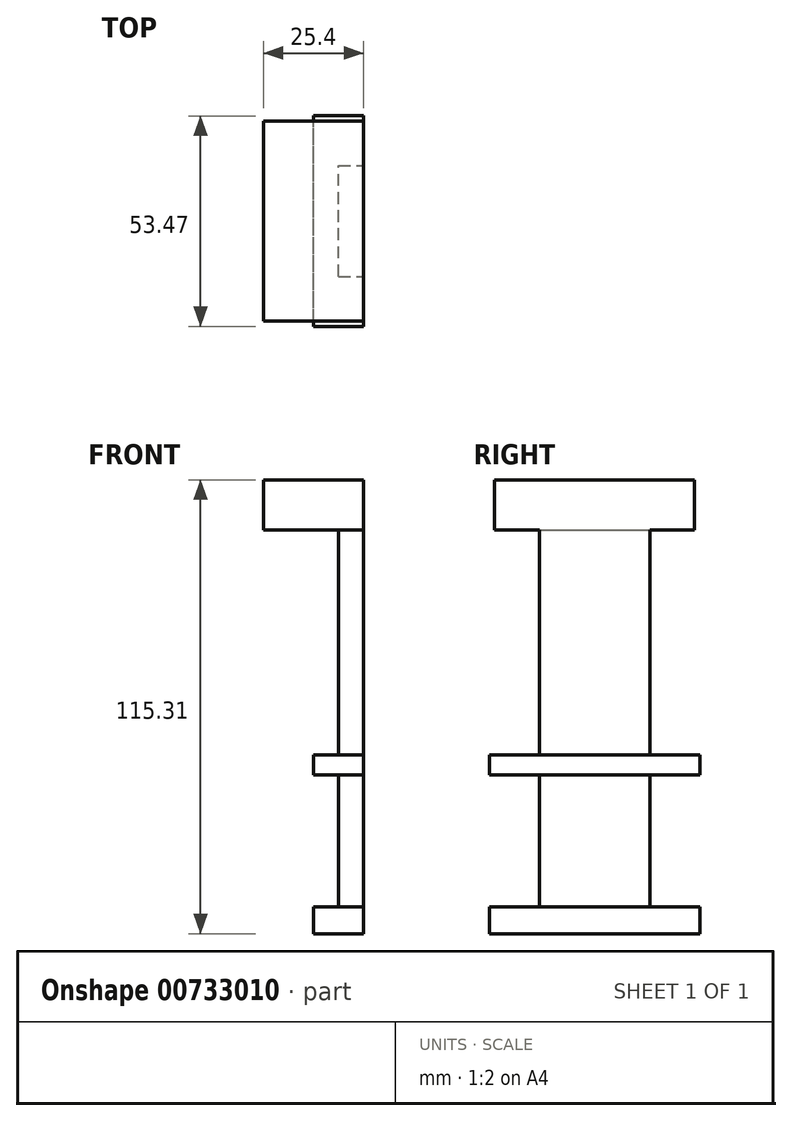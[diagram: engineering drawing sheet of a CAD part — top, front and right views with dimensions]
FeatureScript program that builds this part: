
annotation { "Feature Type Name" : "Feature", "Feature Type Description" : "" }
export const myFeature = defineFeature(function(context is Context, id is Id, definition is map)
    precondition{}
    {
        {
            var Q0;
            Q0=qCreatedBy(makeId("Right.planeOp"),FACE);
            var sketch = newSketch(context, id + "F0", { "sketchPlane" : qUnion([Q0])});
            skLineSegment(sketch, "E0", {"start": v(-21.66, 74) * mm, "end": v(-21.66, 61.3) * mm});
            skLineSegment(sketch, "E1", {"start": v(-21.66, 74) * mm, "end": v(29.14, 74) * mm});
            skLineSegment(sketch, "E2", {"start": v(-21.66, 61.3) * mm, "end": v(29.14, 61.3) * mm});
            skLineSegment(sketch, "E3", {"start": v(29.14, 74) * mm, "end": v(29.14, 61.3) * mm});
            skLineSegment(sketch, "E4", {"start": v(-10.3, 61.3) * mm, "end": v(-10.3, 4.15) * mm});
            skLineSegment(sketch, "E5", {"start": v(17.77, 61.3) * mm, "end": v(17.77, 4.15) * mm});
            skLineSegment(sketch, "E6", {"start": v(-10.3, 4.15) * mm, "end": v(-23, 4.15) * mm});
            skLineSegment(sketch, "E7", {"start": v(-23, 4.15) * mm, "end": v(-23, -0.95) * mm});
            skLineSegment(sketch, "E8", {"start": v(17.77, 4.15) * mm, "end": v(30.47, 4.15) * mm});
            skLineSegment(sketch, "E9", {"start": v(-23, -0.95) * mm, "end": v(30.47, -0.95) * mm});
            skLineSegment(sketch, "E10", {"start": v(30.47, 4.15) * mm, "end": v(30.47, -0.95) * mm});
            skLineSegment(sketch, "E11", {"start": v(-10.3, 4.15) * mm, "end": v(17.77, 4.15) * mm});
            skLineSegment(sketch, "E12", {"start": v(-10.3, -0.95) * mm, "end": v(-10.3, -34.48) * mm});
            skLineSegment(sketch, "E13", {"start": v(17.77, -0.95) * mm, "end": v(17.77, -34.48) * mm});
            skLineSegment(sketch, "E14", {"start": v(-10.3, -34.48) * mm, "end": v(17.77, -34.48) * mm});
            skLineSegment(sketch, "E15", {"start": v(17.77, -34.48) * mm, "end": v(30.47, -34.48) * mm});
            skLineSegment(sketch, "E16", {"start": v(30.47, -34.48) * mm, "end": v(30.47, -41.3) * mm});
            skLineSegment(sketch, "E17", {"start": v(-10.3, -34.48) * mm, "end": v(-23, -34.48) * mm});
            skLineSegment(sketch, "E18", {"start": v(30.47, -41.3) * mm, "end": v(-23, -41.3) * mm});
            skLineSegment(sketch, "E19", {"start": v(-23, -34.48) * mm, "end": v(-23, -41.3) * mm});
            skSolve(sketch);
        }
        {
            var Q0;
            {var subQ3=sQuery(id+"F0.wireOp",EDGE,"E0");Q0=makeQuery(id+"F0.imprint","IMPRINT",FACE,{"disambiguationData":[TD([[makeQuery(id+"F0.imprint","IMPRINT",EDGE,{"derivedFrom":subQ3}),1.0]])]});}
            extrude(context, id + "F1", {"entities" : qUnion([Q0]), "oppositeDirection" : true, "depth" : 25.4 * mm, "offsetDistance" : 25.4 * mm});
        }
        {
            var Q0;
            {var subQ0=sQuery(id+"F0.wireOp",EDGE,"E4");Q0=makeQuery(id+"F0.imprint","IMPRINT",FACE,{"disambiguationData":[TD([[makeQuery(id+"F0.imprint","IMPRINT",EDGE,{"derivedFrom":subQ0}),1.0]])]});}
            var Q1;
            {var subQ0=sQuery(id+"F0.wireOp",EDGE,"E12");Q1=makeQuery(id+"F0.imprint","IMPRINT",FACE,{"disambiguationData":[TD([[makeQuery(id+"F0.imprint","IMPRINT",EDGE,{"derivedFrom":subQ0}),1.0]])]});}
            extrude(context, id + "F2", {"entities" : qUnion([Q0, Q1]), "operationType" : NewBodyOperationType.ADD, "oppositeDirection" : true, "depth" : 6.35 * mm, "offsetDistance" : 25.4 * mm});
        }
        {
            var Q0;
            Q0=makeQuery(id+"F0.imprint","IMPRINT",FACE,{"disambiguationData":[TD([[makeQuery(id+"F0.imprint","IMPRINT",EDGE,{"derivedFrom":sQuery(id+"F0.wireOp",EDGE,"E6")}),1.0]])]});
            var Q1;
            Q1=makeQuery(id+"F0.imprint","IMPRINT",FACE,{"disambiguationData":[TD([[makeQuery(id+"F0.imprint","IMPRINT",EDGE,{"derivedFrom":sQuery(id+"F0.wireOp",EDGE,"E14")}),-1.0]])]});
            extrude(context, id + "F3", {"entities" : qUnion([Q0, Q1]), "oppositeDirection" : true, "depth" : 12.7 * mm, "offsetDistance" : 25.4 * mm});
        }
    });
